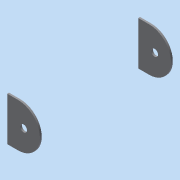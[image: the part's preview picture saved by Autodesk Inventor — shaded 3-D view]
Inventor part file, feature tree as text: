
AUTODESK INVENTOR PART (.ipt)
format: ipt  version: 2015 (Build 190159000, 159)  size: 109,568 bytes
history: native  units: in
note: dims shown in document units (in); Inventor stores cm internally (conversion verified against a paired STEP export)
features: extrude x4, fillet x4, sketch x3, plane x1, other x1
ambient origin geometry x8: Origin, YZ Plane, XZ Plane, XY Plane, X Axis, Y Axis, Z Axis, Center Point
bodies: Solid1 (feature_tree)
feature tree (13):
  extrude  "Extrusion1"  Depth=2.0in
  fillet  "Fillet1"  Radius=0.083in
  plane  "Work Plane2"
  extrude  "Extrusion5"  [1 undecoded]
  fillet  "Fillet3"  Radius=2.0in
  extrude  "Extrusion6"  Depth=1.0in
  extrude  "Extrusion7"  Depth=1.0in
  fillet  "Fillet4"  Radius=1.0in
  fillet  "Fillet5"  Radius=0.75in
  other  "Side Element"
  sketch  "Sketch6"  dims[d0=1.5in d1=2.0in d2=0.083in d3=0.0in]
  sketch  "Sketch7"  dims[d4=1.0in d22=-6.0in d23=2.0in]
  sketch  "Sketch8"  dims[d24=0.083in d25=0.0in d26=1.0in d27=0.315in d28=1.0in d29=0.75in d30=0.083in d31=0.0in d32=0.315in d33=1.0in d34=0.75in d35=0.083in d36=0.0in d37=1.0in d38=1.0in]
note: 1 required parameter value undecoded (feature->parameter linkage not recoverable at this tier; creation-order binding heuristic only, values carry confidence <= 0.55)
